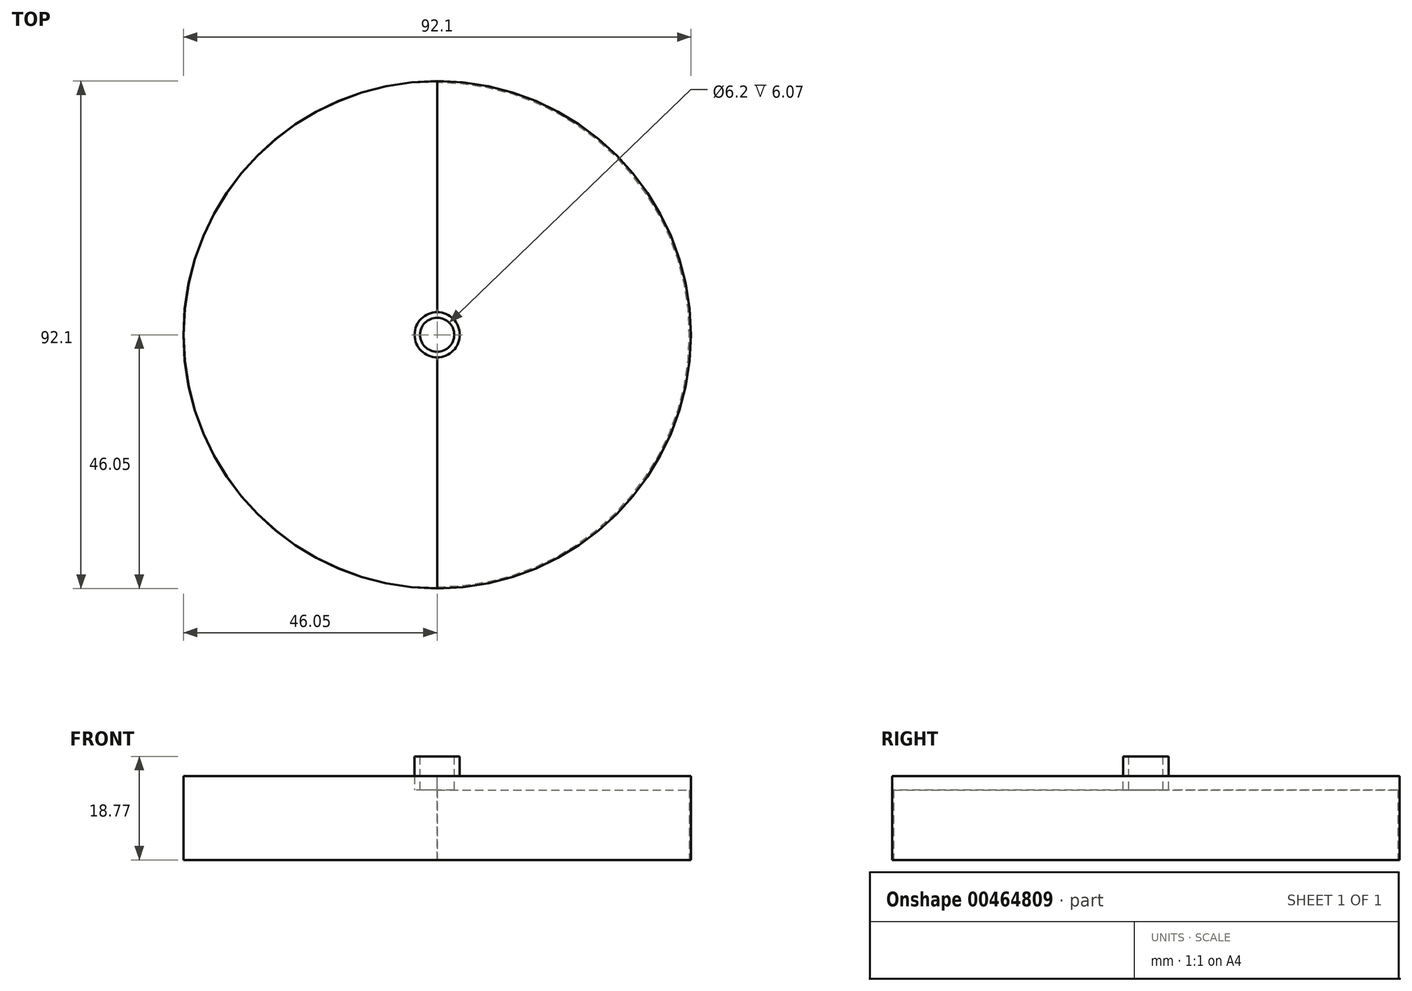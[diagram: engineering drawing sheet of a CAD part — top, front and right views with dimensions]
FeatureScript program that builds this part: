
annotation { "Feature Type Name" : "Feature", "Feature Type Description" : "" }
export const myFeature = defineFeature(function(context is Context, id is Id, definition is map)
    precondition{}
    {
        {
            var Q0;
            Q0=qCreatedBy(makeId("Top.planeOp"),FACE);
            var sketch = newSketch(context, id + "F0", { "sketchPlane" : qUnion([Q0])});
            skCircle(sketch, "E0", {"center": v(0, 0) * mm, "radius": 46.05 * mm});
            skSolve(sketch);
        }
        {
            var Q0;
            Q0=qSketchRegion(id+"F0",true);
            extrude(context, id + "F1", {"entities" : qUnion([Q0]), "depth" : 15.24 * mm});
        }
        {
            var Q0;
            Q0=qCreatedBy(makeId("Top.planeOp"),FACE);
            var sketch = newSketch(context, id + "F2", { "sketchPlane" : qUnion([Q0])});
            skCircle(sketch, "E1", {"center": v(0, 0) * mm, "radius": 46.05 * mm});
            skCircle(sketch, "E2.0", {"center": v(0, 0) * mm, "radius": 46.05 * mm, "construction": true});
            skCircle(sketch, "E3", {"center": v(0, 0) * mm, "radius": 45.75 * mm});
            skSolve(sketch);
        }
        {
            var Q0;
            Q0=makeQuery(id+"F2.imprint","IMPRINT",FACE,{"disambiguationData":[TD([[makeQuery(id+"F2.imprint","IMPRINT",EDGE,{"derivedFrom":sQuery(id+"F2.wireOp",EDGE,"E3")}),1.0]])]});
            extrude(context, id + "F3", {"entities" : qUnion([Q0]), "operationType" : NewBodyOperationType.REMOVE, "depth" : 12.7 * mm});
        }
        {
            var Q0;
            Q0=makeQuery(id+"F1.opExtrude","CAP_FACE",FACE,{"disambiguationData":[OSD([sQuery(id+"F0.wireOp",EDGE,"E0")])],"isStart":false});
            var sketch = newSketch(context, id + "F4", { "sketchPlane" : qUnion([Q0])});
            skCircle(sketch, "E4", {"center": v(0, 0) * mm, "radius": 4.1 * mm});
            skSolve(sketch);
        }
        {
            var Q0;
            Q0=makeQuery(id+"F4.imprint","IMPRINT",FACE,{"disambiguationData":[TD([[makeQuery(id+"F4.imprint","IMPRINT",EDGE,{"derivedFrom":sQuery(id+"F4.wireOp",EDGE,"E4")}),1.0]])]});
            extrude(context, id + "F5", {"entities" : qUnion([Q0]), "operationType" : NewBodyOperationType.ADD, "depth" : 3.53 * mm, "hasSecondDirection" : true, "secondDirectionOppositeDirection" : true, "secondDirectionDepth" : 1 * mm});
        }
        {
            var Q0;
            Q0=makeQuery(id+"F1.opExtrude","CAP_FACE",FACE,{"disambiguationData":[OSD([sQuery(id+"F0.wireOp",EDGE,"E0")])],"isStart":false});
            var sketch = newSketch(context, id + "F6", { "sketchPlane" : qUnion([Q0])});
            skCircle(sketch, "E5.0", {"center": v(0, 0) * mm, "radius": 46.05 * mm});
            skArc(sketch, "E6", {"start": v(0, 46.03) * mm, "mid": v(-46.03, 0) * mm, "end": v(0, -46.03) * mm});
            skLineSegment(sketch, "E7", {"start": v(0, 46.03) * mm, "end": v(0, -46.03) * mm});
            skSolve(sketch);
        }
        {
            var Q0;
            Q0=makeQuery(id+"F6.imprint","IMPRINT",FACE,{"disambiguationData":[TD([[makeQuery(id+"F6.imprint","IMPRINT",EDGE,{"derivedFrom":sQuery(id+"F6.wireOp",EDGE,"E6")}),1.0]])]});
            extrude(context, id + "F7", {"entities" : qUnion([Q0]), "operationType" : NewBodyOperationType.REMOVE, "endBound" : BoundingType.THROUGH_ALL, "oppositeDirection" : true, "depth" : 25.4 * mm});
        }
        {
            var Q0;
            Q0=makeQuery(id+"F5.opExtrude","CAP_FACE",FACE,{"disambiguationData":[OSD([sQuery(id+"F4.wireOp",EDGE,"E4")])],"isStart":false});
            var sketch = newSketch(context, id + "F8", { "sketchPlane" : qUnion([Q0])});
            skCircle(sketch, "E8", {"center": v(0, 0) * mm, "radius": 3.1 * mm});
            skSolve(sketch);
        }
        {
            var Q0;
            Q0=makeQuery(id+"F8.imprint","IMPRINT",FACE,{"disambiguationData":[TD([[makeQuery(id+"F8.imprint","IMPRINT",EDGE,{"derivedFrom":sQuery(id+"F8.wireOp",EDGE,"E8")}),1.0]])]});
            extrude(context, id + "F9", {"entities" : qUnion([Q0]), "operationType" : NewBodyOperationType.REMOVE, "endBound" : BoundingType.THROUGH_ALL, "oppositeDirection" : true, "depth" : 25.4 * mm});
        }
    });
